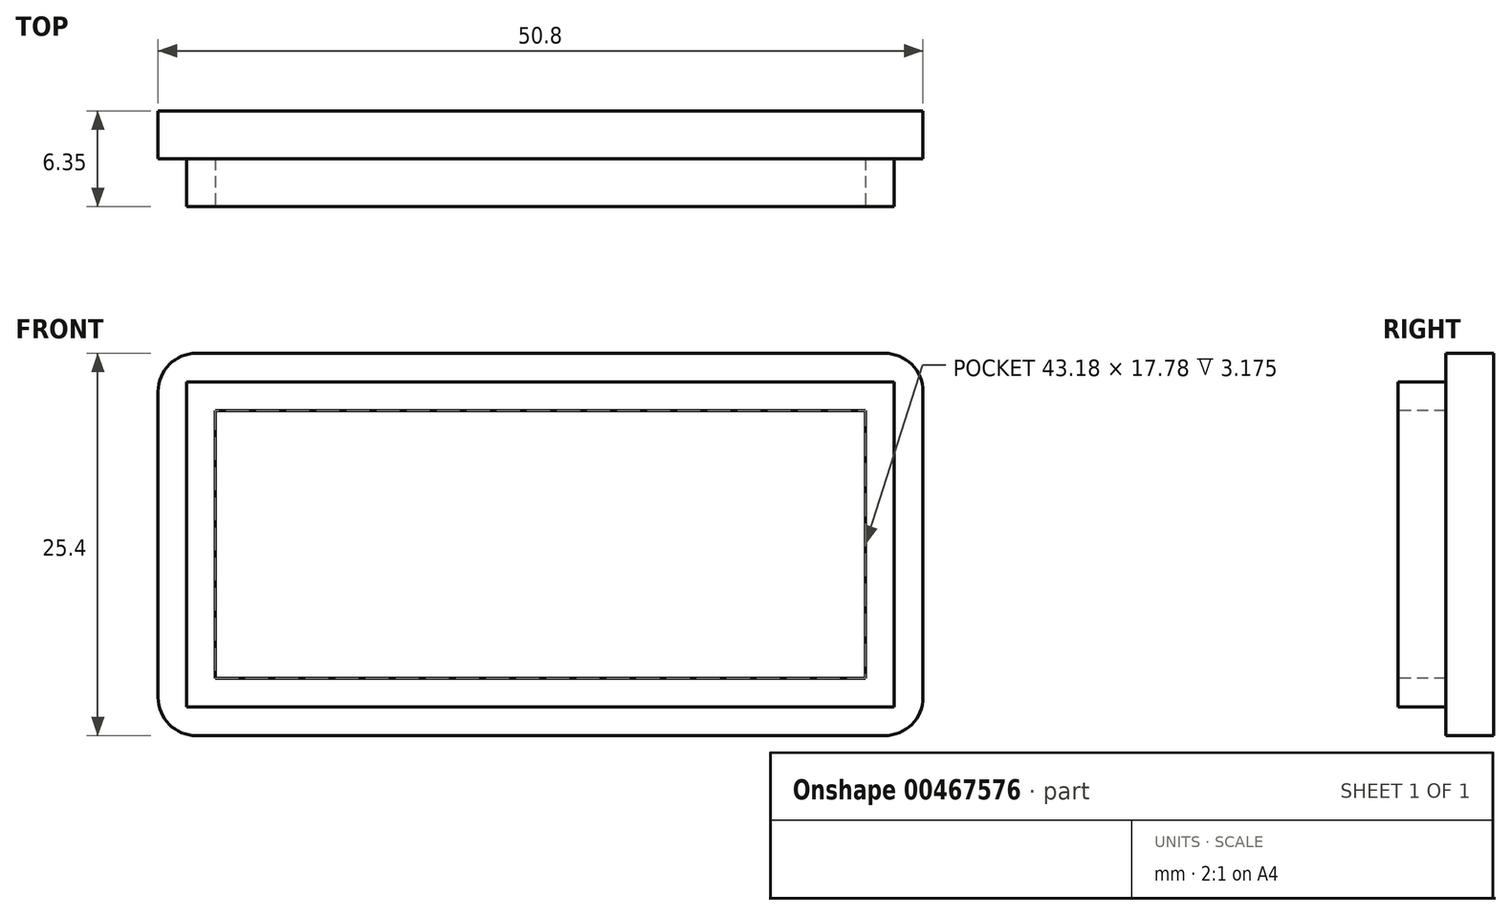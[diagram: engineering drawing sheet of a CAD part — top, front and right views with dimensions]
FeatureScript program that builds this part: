
annotation { "Feature Type Name" : "Feature", "Feature Type Description" : "" }
export const myFeature = defineFeature(function(context is Context, id is Id, definition is map)
    precondition{}
    {
        {
            var Q0;
            Q0=qCreatedBy(makeId("Front.planeOp"),FACE);
            var sketch = newSketch(context, id + "F0", { "sketchPlane" : qUnion([Q0])});
            skLineSegment(sketch, "E0.bottom", {"start": v(-23.81, -11.11) * mm, "end": v(23.81, -11.11) * mm});
            skLineSegment(sketch, "E0.top", {"start": v(-23.81, 11.11) * mm, "end": v(23.81, 11.11) * mm});
            skLineSegment(sketch, "E0.left", {"start": v(-23.81, -11.11) * mm, "end": v(-23.81, 11.11) * mm});
            skLineSegment(sketch, "E0.right", {"start": v(23.81, -11.11) * mm, "end": v(23.81, 11.11) * mm});
            skPoint(sketch, "E0.middle", {"position": v(0, 0) * mm});
            skLineSegment(sketch, "E1.bottom", {"start": v(-25.4, -12.7) * mm, "end": v(25.4, -12.7) * mm});
            skLineSegment(sketch, "E1.top", {"start": v(-25.4, 12.7) * mm, "end": v(25.4, 12.7) * mm});
            skLineSegment(sketch, "E1.left", {"start": v(-25.4, -12.7) * mm, "end": v(-25.4, 12.7) * mm});
            skLineSegment(sketch, "E1.right", {"start": v(25.4, -12.7) * mm, "end": v(25.4, 12.7) * mm});
            skSolve(sketch);
        }
        {
            var Q0;
            Q0 = qSketchRegion(id + "F0", true);
            var Q1;
            Q1=makeQuery(id+"F0.imprint","IMPRINT",FACE,{"disambiguationData":[TD([[makeQuery(id+"F0.imprint","IMPRINT",EDGE,{"derivedFrom":sQuery(id+"F0.wireOp",EDGE,"E0.bottom")}),1.0]])]});
            extrude(context, id + "F1", {"entities" : qUnion([Q0, Q1]), "depth" : 3.17 * mm});
        }
        {
            var Q0;
            Q0=makeQuery(id+"F1.opExtrude","CAP_FACE",FACE,{"disambiguationData":[OSD([sQuery(id+"F0.wireOp",EDGE,"E1.bottom"),sQuery(id+"F0.wireOp",EDGE,"E1.top"),sQuery(id+"F0.wireOp",EDGE,"E1.left"),sQuery(id+"F0.wireOp",EDGE,"E1.right")])],"isStart":false});
            var sketch = newSketch(context, id + "F2", { "sketchPlane" : qUnion([Q0])});
            skLineSegment(sketch, "E2.bottom", {"start": v(23.5, -10.8) * mm, "end": v(-23.5, -10.8) * mm});
            skLineSegment(sketch, "E2.top", {"start": v(23.5, 10.8) * mm, "end": v(-23.5, 10.8) * mm});
            skLineSegment(sketch, "E2.left", {"start": v(23.5, -10.8) * mm, "end": v(23.5, 10.8) * mm});
            skLineSegment(sketch, "E2.right", {"start": v(-23.5, -10.8) * mm, "end": v(-23.5, 10.8) * mm});
            skPoint(sketch, "E2.middle", {"position": v(0, 0) * mm});
            skSolve(sketch);
        }
        {
            var Q0;
            Q0=makeQuery(id+"F2.imprint","IMPRINT",FACE,{"disambiguationData":[TD([[makeQuery(id+"F2.imprint","IMPRINT",EDGE,{"derivedFrom":sQuery(id+"F2.wireOp",EDGE,"E2.bottom")}),-1.0]])]});
            extrude(context, id + "F3", {"entities" : qUnion([Q0]), "operationType" : NewBodyOperationType.ADD, "depth" : 3.17 * mm});
        }
        {
            var Q0;
            Q0=makeQuery(id+"F3.opExtrude","CAP_FACE",FACE,{"disambiguationData":[OSD([sQuery(id+"F2.wireOp",EDGE,"E2.bottom"),sQuery(id+"F2.wireOp",EDGE,"E2.top"),sQuery(id+"F2.wireOp",EDGE,"E2.left"),sQuery(id+"F2.wireOp",EDGE,"E2.right")])],"isStart":false});
            var sketch = newSketch(context, id + "F4", { "sketchPlane" : qUnion([Q0])});
            skLineSegment(sketch, "E3.bottom", {"start": v(21.59, -8.89) * mm, "end": v(-21.59, -8.9) * mm});
            skLineSegment(sketch, "E3.top", {"start": v(21.59, 8.9) * mm, "end": v(-21.59, 8.89) * mm});
            skLineSegment(sketch, "E3.left", {"start": v(21.59, -8.89) * mm, "end": v(21.59, 8.9) * mm});
            skLineSegment(sketch, "E3.right", {"start": v(-21.59, -8.9) * mm, "end": v(-21.59, 8.89) * mm});
            skPoint(sketch, "E3.middle", {"position": v(0, 0) * mm});
            skSolve(sketch);
        }
        {
            var Q0;
            Q0 = qSketchRegion(id + "F4", true);
            extrude(context, id + "F5", {"entities" : qUnion([Q0]), "operationType" : NewBodyOperationType.REMOVE, "oppositeDirection" : true, "depth" : 3.17 * mm});
        }
        {
            var Q0;
            Q0=makeQuery(id+"F1.opExtrude","SWEPT_EDGE",EDGE,{"disambiguationData":[OSD([sQuery(id+"F0.wireOp",EDGE,"E1.bottom"),sQuery(id+"F0.wireOp",EDGE,"E1.left")])]});
            var Q1;
            Q1=makeQuery(id+"F1.opExtrude","SWEPT_EDGE",EDGE,{"disambiguationData":[OSD([sQuery(id+"F0.wireOp",EDGE,"E1.bottom"),sQuery(id+"F0.wireOp",EDGE,"E1.right")])]});
            var Q2;
            Q2=makeQuery(id+"F1.opExtrude","SWEPT_EDGE",EDGE,{"disambiguationData":[OSD([sQuery(id+"F0.wireOp",EDGE,"E1.top"),sQuery(id+"F0.wireOp",EDGE,"E1.right")])]});
            var Q3;
            Q3=makeQuery(id+"F1.opExtrude","SWEPT_EDGE",EDGE,{"disambiguationData":[OSD([sQuery(id+"F0.wireOp",EDGE,"E1.top"),sQuery(id+"F0.wireOp",EDGE,"E1.left")])]});
            fillet(context, id + "F6", {"entities" : qUnion([Q0, Q1, Q2, Q3]), "radius" : 2.54 * mm, "tangentPropagation" : true, "allowEdgeOverflow" : false});
        }
    });
